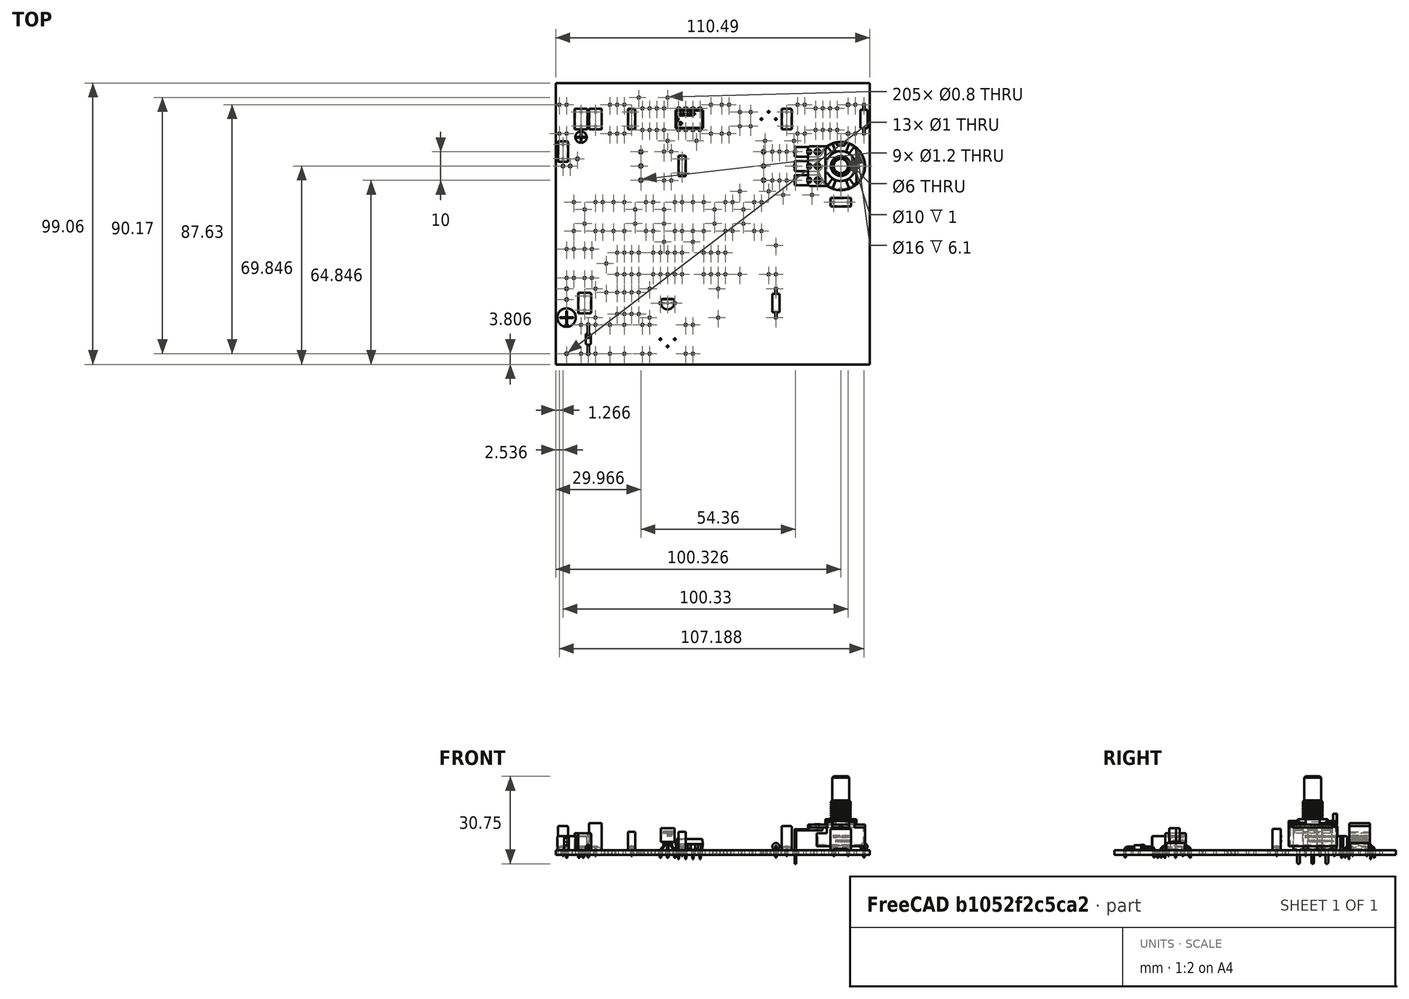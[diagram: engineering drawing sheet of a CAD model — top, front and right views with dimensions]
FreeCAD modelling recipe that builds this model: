
FCSTD DOCUMENT  (FreeCAD 0.19R17089 +1543 (Git))
Label: Board Reproduction
License: All rights reserved
LicenseURL: http://en.wikipedia.org/wiki/All_rights_reserved
objects: App::Link×70, Part::Feature×19, App::Part×4, PartDesign::CoordinateSystem×1, Sketcher::SketchObject×1
note: 21 computed .brp shape members not serialized (recipe doc carries the construction recipe); baked Part::Feature solids carry a one-line shape summary decoded from their .brp

FEATURE [PartDesign::CoordinateSystem] Local_CS
  AttacherType = Attacher::AttachEngine3D
FEATURE [Part::Feature] Pcb
  Placement = pos=(-148.5,98.5,0) rot=(0,0,1;0rad)
  shape: bbox 110.5 x 99.06 x 1.6 mm, 246 faces (baked)
FEATURE [Sketcher::SketchObject] PCB_Sketch
  sketch-geometry (10):
    g0: LineSegment StartX=-61.124 StartY=53.796 StartZ=0 EndX=-61.124 EndY=52.526 EndZ=0
    g1: LineSegment StartX=-25.564 StartY=53.796 StartZ=0 EndX=-61.124 EndY=53.796 EndZ=0
    g2: LineSegment StartX=49.366 StartY=53.796 StartZ=0 EndX=-25.564 EndY=53.796 EndZ=0
    g3: LineSegment StartX=49.366 StartY=-45.264 StartZ=0 EndX=49.366 EndY=53.796 EndZ=0
    g4: LineSegment StartX=-5.244 StartY=-45.264 StartZ=0 EndX=49.366 EndY=-45.264 EndZ=0
    g5: LineSegment StartX=-53.504 StartY=-45.264 StartZ=0 EndX=-5.244 EndY=-45.264 EndZ=0
    g6: LineSegment StartX=-61.124 StartY=-45.264 StartZ=0 EndX=-53.504 EndY=-45.264 EndZ=0
    g7: LineSegment StartX=-61.124 StartY=-38.914 StartZ=0 EndX=-61.124 EndY=-45.264 EndZ=0
    g8: LineSegment StartX=-61.124 StartY=1.726 StartZ=0 EndX=-61.124 EndY=52.526 EndZ=0
    g9: LineSegment StartX=-61.124 StartY=-38.914 StartZ=0 EndX=-61.124 EndY=1.726 EndZ=0
  constraints (10):
    c: Coincident(g6,g7)
    c: Coincident(g7,g9)
    c: Coincident(g8,g9)
    c: Coincident(g0,g8)
    c: Coincident(g0,g1)
    c: Coincident(g5,g6)
    c: Coincident(g1,g2)
    c: Coincident(g4,g5)
    c: Coincident(g3,g4)
    c: Coincident(g2,g3)
FEATURE [Part::Feature] Shape  label="C15_Nichicon_UMA_Straight_D6.5_H5_P2.5_d0.45_LL2.6_5D8C32D9"
  Placement = pos=(-57.314,-28.754,0) rot=(0,0,1;3.14159rad)
  shape: bbox 7.036 x 7.036 x 7.61 mm, 57 faces (baked)
FEATURE [Part::Feature] Shape001  label="C13_Nichicon_UMA_Straight_D4_H5_P1.5_d0.45_LL2.6_5D8A0658"
  Placement = pos=(-52.234,34.746,0) rot=(0,0,-1;1.5708rad)
  shape: bbox 4.33 x 4.33 x 7.61 mm, 61 faces (baked)
FEATURE [Part::Feature] Shape002  label="Q1_2N3904TAR_5D8C3344"
  Placement = pos=(-21.754,-23.674,0) rot=(0,0,1;3.14159rad)
  shape: bbox 5.54 x 3.625 x 10.42 mm, 233 faces (baked)
FEATURE [Part::Feature] Shape003  label="JP12_R_CF25_P10.16_H_5D8B2718"
  Placement = pos=(16.346,-23.674,0) rot=(0,0,1;1.5708rad)
  shape: bbox 2.5 x 10.96 x 5.1 mm, 11 faces (baked)
FEATURE [App::Link] JP12_R_CF25_P10_16_H_5D8B2718_ln_  label="JP11_R_CF25_P10.16_H_5D8B2701"
  LinkPlacement = pos=(23.966,14.426,0) rot=(0,0,1;3.14159rad)
  LinkedObject = -> Shape003
  Placement = pos=(23.966,14.426,0) rot=(0,0,1;3.14159rad)
FEATURE [App::Link] JP12_R_CF25_P10_16_H_5D8B2718_ln_001  label="JP10_R_CF25_P10.16_H_5D8B26EA"
  LinkPlacement = pos=(8.726,15.696,0) rot=(0,0,1;3.14159rad)
  LinkedObject = -> Shape003
  Placement = pos=(8.726,15.696,0) rot=(0,0,1;3.14159rad)
FEATURE [App::Link] JP12_R_CF25_P10_16_H_5D8B2718_ln_002  label="JP9_R_CF25_P10.16_H_5D8DF354"
  LinkPlacement = pos=(16.346,-8.434,0) rot=(0,0,1;1.5708rad)
  LinkedObject = -> Shape003
  Placement = pos=(16.346,-8.434,0) rot=(0,0,1;1.5708rad)
FEATURE [App::Link] JP12_R_CF25_P10_16_H_5D8B2718_ln_003  label="JP8_R_CF25_P10.16_H_5D8C9031"
  LinkPlacement = pos=(8.726,-13.514,0) rot=(0,0,1;3.14159rad)
  LinkedObject = -> Shape003
  Placement = pos=(8.726,-13.514,0) rot=(0,0,1;3.14159rad)
FEATURE [App::Link] JP12_R_CF25_P10_16_H_5D8B2718_ln_004  label="JP7_R_CF25_P10.16_H_5D8C3305"
  LinkPlacement = pos=(-3.974,-23.674,0) rot=(0,0,-1;1.5708rad)
  LinkedObject = -> Shape003
  Placement = pos=(-3.974,-23.674,0) rot=(0,0,-1;1.5708rad)
FEATURE [App::Link] JP12_R_CF25_P10_16_H_5D8B2718_ln_005  label="JP6_R_CF25_P10.16_H_5D8B268E"
  LinkPlacement = pos=(-17.944,-2.084,0) rot=(0,0,1;3.14159rad)
  LinkedObject = -> Shape003
  Placement = pos=(-17.944,-2.084,0) rot=(0,0,1;3.14159rad)
FEATURE [App::Link] JP12_R_CF25_P10_16_H_5D8B2718_ln_006  label="JP5_R_CF25_P10.16_H_5D8B2677"
  LinkPlacement = pos=(-28.104,-23.674,0) rot=(0,0,1;1.5708rad)
  LinkedObject = -> Shape003
  Placement = pos=(-28.104,-23.674,0) rot=(0,0,1;1.5708rad)
FEATURE [App::Link] JP12_R_CF25_P10_16_H_5D8B2718_ln_007  label="JP4_R_CF25_P10.16_H_5D8B2660"
  LinkPlacement = pos=(-43.344,-14.784,0) rot=(0,0,1;1.5708rad)
  LinkedObject = -> Shape003
  Placement = pos=(-43.344,-14.784,0) rot=(0,0,1;1.5708rad)
FEATURE [App::Link] JP12_R_CF25_P10_16_H_5D8B2718_ln_008  label="JP3_R_CF25_P10.16_H_5D8B2649"
  LinkPlacement = pos=(17.616,33.476,0) rot=(0,0,1;0rad)
  LinkedObject = -> Shape003
  Placement = pos=(17.616,33.476,0) rot=(0,0,1;0rad)
FEATURE [App::Link] JP12_R_CF25_P10_16_H_5D8B2718_ln_009  label="JP2_R_CF25_P10.16_H_5D8B2632"
  LinkPlacement = pos=(-16.674,33.476,0) rot=(0,0,1;0rad)
  LinkedObject = -> Shape003
  Placement = pos=(-16.674,33.476,0) rot=(0,0,1;0rad)
FEATURE [App::Link] JP12_R_CF25_P10_16_H_5D8B2718_ln_010  label="JP1_R_CF25_P10.16_H_5D8B261B"
  LinkPlacement = pos=(-26.834,48.716,0) rot=(0,0,1;0rad)
  LinkedObject = -> Shape003
  Placement = pos=(-26.834,48.716,0) rot=(0,0,1;0rad)
FEATURE [Part::Feature] Shape004  label="R57_R_CC25_P10.16_H_5D8A0B50"
  Placement = pos=(47.334,41.096,0) rot=(0,0,1;1.5708rad)
  shape: bbox 2.5 x 10.96 x 5.1 mm, 11 faces (baked)
FEATURE [App::Link] R57_R_CC25_P10_16_H_5D8A0B50_ln_  label="R56_R_CC25_P10.16_H_5D8A0B39"
  LinkPlacement = pos=(44.286,41.096,0) rot=(0,0,-1;1.5708rad)
  LinkedObject = -> Shape004
  Placement = pos=(44.286,41.096,0) rot=(0,0,-1;1.5708rad)
FEATURE [App::Link] R57_R_CC25_P10_16_H_5D8A0B50_ln_001  label="R45_R_CC25_P10.16_H_5D8A0B22"
  LinkPlacement = pos=(-28.104,-36.374,0) rot=(0,0,-1;1.5708rad)
  LinkedObject = -> Shape004
  Placement = pos=(-28.104,-36.374,0) rot=(0,0,-1;1.5708rad)
FEATURE [App::Link] R57_R_CC25_P10_16_H_5D8A0B50_ln_002  label="R44_R_CC25_P10.16_H_5D8A0B0B"
  LinkPlacement = pos=(-47.154,-36.374,0) rot=(0,0,-1;1.5708rad)
  LinkedObject = -> Shape004
  Placement = pos=(-47.154,-36.374,0) rot=(0,0,-1;1.5708rad)
FEATURE [App::Link] R57_R_CC25_P10_16_H_5D8A0B50_ln_003  label="R43_R_CC25_P10.16_H_5D8A0AF4"
  LinkPlacement = pos=(-30.644,-36.374,0) rot=(0,0,-1;1.5708rad)
  LinkedObject = -> Shape004
  Placement = pos=(-30.644,-36.374,0) rot=(0,0,-1;1.5708rad)
FEATURE [App::Link] R57_R_CC25_P10_16_H_5D8A0B50_ln_004  label="R42_R_CC25_P10.16_H_5D8BE438"
  LinkPlacement = pos=(-42.074,-36.374,0) rot=(0,0,-1;1.5708rad)
  LinkedObject = -> Shape004
  Placement = pos=(-42.074,-36.374,0) rot=(0,0,-1;1.5708rad)
FEATURE [App::Link] R57_R_CC25_P10_16_H_5D8A0B50_ln_005  label="R41_R_CC25_P10.16_H_5D8A0AC6"
  LinkPlacement = pos=(-36.994,-36.374,0) rot=(0,0,-1;1.5708rad)
  LinkedObject = -> Shape004
  Placement = pos=(-36.994,-36.374,0) rot=(0,0,-1;1.5708rad)
FEATURE [App::Link] R57_R_CC25_P10_16_H_5D8A0B50_ln_006  label="R39_R_CC25_P10.16_H_5D8A0AAF"
  LinkPlacement = pos=(-15.404,-36.374,0) rot=(0,0,-1;1.5708rad)
  LinkedObject = -> Shape004
  Placement = pos=(-15.404,-36.374,0) rot=(0,0,-1;1.5708rad)
FEATURE [App::Link] R57_R_CC25_P10_16_H_5D8A0B50_ln_007  label="R37_R_CC25_P10.16_H_5D8A0A98"
  LinkPlacement = pos=(-12.864,-36.374,0) rot=(0,0,-1;1.5708rad)
  LinkedObject = -> Shape004
  Placement = pos=(-12.864,-36.374,0) rot=(0,0,-1;1.5708rad)
FEATURE [App::Link] R57_R_CC25_P10_16_H_5D8A0B50_ln_008  label="R36_R_CC25_P10.16_H_5D8A0A81"
  LinkPlacement = pos=(15.076,24.586,0) rot=(0,0,-1;1.5708rad)
  LinkedObject = -> Shape004
  Placement = pos=(15.076,24.586,0) rot=(0,0,-1;1.5708rad)
FEATURE [App::Link] R57_R_CC25_P10_16_H_5D8A0B50_ln_009  label="R35_R_CC25_P10.16_H_5D8A0A6A"
  LinkPlacement = pos=(20.156,24.586,0) rot=(0,0,-1;1.5708rad)
  LinkedObject = -> Shape004
  Placement = pos=(20.156,24.586,0) rot=(0,0,-1;1.5708rad)
FEATURE [App::Link] R57_R_CC25_P10_16_H_5D8A0B50_ln_010  label="R34_R_CC25_P10.16_H_5D8A0A53"
  LinkPlacement = pos=(17.616,24.586,0) rot=(0,0,-1;1.5708rad)
  LinkedObject = -> Shape004
  Placement = pos=(17.616,24.586,0) rot=(0,0,-1;1.5708rad)
FEATURE [App::Link] R57_R_CC25_P10_16_H_5D8A0B50_ln_011  label="R33_R_CC25_P10.16_H_5D8A0A3C"
  LinkPlacement = pos=(26.506,41.096,0) rot=(0,0,1;1.5708rad)
  LinkedObject = -> Shape004
  Placement = pos=(26.506,41.096,0) rot=(0,0,1;1.5708rad)
FEATURE [App::Link] R57_R_CC25_P10_16_H_5D8A0B50_ln_012  label="R32_R_CC25_P10.16_H_5D8A0A25"
  LinkPlacement = pos=(23.966,41.096,0) rot=(0,0,-1;1.5708rad)
  LinkedObject = -> Shape004
  Placement = pos=(23.966,41.096,0) rot=(0,0,-1;1.5708rad)
FEATURE [App::Link] R57_R_CC25_P10_16_H_5D8A0B50_ln_013  label="R31_R_CC25_P10.16_H_5D8A0A0E"
  LinkPlacement = pos=(-52.234,-36.374,0) rot=(0,0,-1;1.5708rad)
  LinkedObject = -> Shape004
  Placement = pos=(-52.234,-36.374,0) rot=(0,0,-1;1.5708rad)
FEATURE [App::Link] R57_R_CC25_P10_16_H_5D8A0B50_ln_014  label="R30_R_CC25_P10.16_H_5D8C3383"
  LinkPlacement = pos=(-47.154,-23.674,0) rot=(0,0,1;1.5708rad)
  LinkedObject = -> Shape004
  Placement = pos=(-47.154,-23.674,0) rot=(0,0,1;1.5708rad)
FEATURE [App::Link] R57_R_CC25_P10_16_H_5D8A0B50_ln_015  label="R29_R_CC25_P10.16_H_5D8A09E0"
  LinkPlacement = pos=(-54.774,-9.704,0) rot=(0,0,-1;1.5708rad)
  LinkedObject = -> Shape004
  Placement = pos=(-54.774,-9.704,0) rot=(0,0,-1;1.5708rad)
FEATURE [App::Link] R57_R_CC25_P10_16_H_5D8A0B50_ln_016  label="R28_R_CC25_P10.16_H_5D8A09C9"
  LinkPlacement = pos=(-57.314,-9.704,0) rot=(0,0,1;1.5708rad)
  LinkedObject = -> Shape004
  Placement = pos=(-57.314,-9.704,0) rot=(0,0,1;1.5708rad)
FEATURE [App::Link] R57_R_CC25_P10_16_H_5D8A0B50_ln_017  label="R27_R_CC25_P10.16_H_5D8A09B2"
  LinkPlacement = pos=(-50.964,-9.704,0) rot=(0,0,1;1.5708rad)
  LinkedObject = -> Shape004
  Placement = pos=(-50.964,-9.704,0) rot=(0,0,1;1.5708rad)
FEATURE [App::Link] R57_R_CC25_P10_16_H_5D8A0B50_ln_018  label="R26_R_CC25_P10.16_H_5D8A099B"
  LinkPlacement = pos=(-48.424,-9.704,0) rot=(0,0,1;1.5708rad)
  LinkedObject = -> Shape004
  Placement = pos=(-48.424,-9.704,0) rot=(0,0,1;1.5708rad)
FEATURE [App::Link] R57_R_CC25_P10_16_H_5D8A0B50_ln_019  label="R25_R_CC25_P10.16_H_5D8B716B"
  LinkPlacement = pos=(11.266,6.806,0) rot=(0,0,-1;1.5708rad)
  LinkedObject = -> Shape004
  Placement = pos=(11.266,6.806,0) rot=(0,0,-1;1.5708rad)
FEATURE [App::Link] R57_R_CC25_P10_16_H_5D8A0B50_ln_020  label="R24_R_CC25_P10.16_H_5D8A096D"
  LinkPlacement = pos=(-0.164,41.096,0) rot=(0,0,1;1.5708rad)
  LinkedObject = -> Shape004
  Placement = pos=(-0.164,41.096,0) rot=(0,0,1;1.5708rad)
FEATURE [App::Link] R57_R_CC25_P10_16_H_5D8A0B50_ln_021  label="R23_R_CC25_P10.16_H_5D8A0956"
  LinkPlacement = pos=(-2.704,41.096,0) rot=(0,0,-1;1.5708rad)
  LinkedObject = -> Shape004
  Placement = pos=(-2.704,41.096,0) rot=(0,0,-1;1.5708rad)
FEATURE [App::Link] R57_R_CC25_P10_16_H_5D8A0B50_ln_022  label="R22_R_CC25_P10.16_H_5D8B6ED7"
  LinkPlacement = pos=(8.726,6.806,0) rot=(0,0,-1;1.5708rad)
  LinkedObject = -> Shape004
  Placement = pos=(8.726,6.806,0) rot=(0,0,-1;1.5708rad)
FEATURE [App::Link] R57_R_CC25_P10_16_H_5D8A0B50_ln_023  label="R21_R_CC25_P10.16_H_5D8A0928"
  LinkPlacement = pos=(-6.514,41.096,0) rot=(0,0,-1;1.5708rad)
  LinkedObject = -> Shape004
  Placement = pos=(-6.514,41.096,0) rot=(0,0,-1;1.5708rad)
FEATURE [App::Link] R57_R_CC25_P10_16_H_5D8A0B50_ln_024  label="R20_R_CC25_P10.16_H_5D8B7021"
  LinkPlacement = pos=(1.106,6.806,0) rot=(0,0,-1;1.5708rad)
  LinkedObject = -> Shape004
  Placement = pos=(1.106,6.806,0) rot=(0,0,-1;1.5708rad)
FEATURE [App::Link] R57_R_CC25_P10_16_H_5D8A0B50_ln_025  label="R19_R_CC25_P10.16_H_5D8C3024"
  LinkPlacement = pos=(-1.434,6.806,0) rot=(0,0,1;1.5708rad)
  LinkedObject = -> Shape004
  Placement = pos=(-1.434,6.806,0) rot=(0,0,1;1.5708rad)
FEATURE [App::Link] R57_R_CC25_P10_16_H_5D8A0B50_ln_026  label="R18_R_CC25_P10.16_H_5D8B70E7"
  LinkPlacement = pos=(-9.054,6.806,0) rot=(0,0,-1;1.5708rad)
  LinkedObject = -> Shape004
  Placement = pos=(-9.054,6.806,0) rot=(0,0,-1;1.5708rad)
FEATURE [App::Link] R57_R_CC25_P10_16_H_5D8A0B50_ln_027  label="R17_R_CC25_P10.16_H_5D8B6E95"
  LinkPlacement = pos=(-12.864,6.806,0) rot=(0,0,-1;1.5708rad)
  LinkedObject = -> Shape004
  Placement = pos=(-12.864,6.806,0) rot=(0,0,-1;1.5708rad)
FEATURE [App::Link] R57_R_CC25_P10_16_H_5D8A0B50_ln_028  label="R16_R_CC25_P10.16_H_5D8B6F9D"
  LinkPlacement = pos=(-19.214,6.806,0) rot=(0,0,1;1.5708rad)
  LinkedObject = -> Shape004
  Placement = pos=(-19.214,6.806,0) rot=(0,0,1;1.5708rad)
FEATURE [App::Link] R57_R_CC25_P10_16_H_5D8A0B50_ln_029  label="R15_R_CC25_P10.16_H_5D8B6FDF"
  LinkPlacement = pos=(-16.674,6.806,0) rot=(0,0,-1;1.5708rad)
  LinkedObject = -> Shape004
  Placement = pos=(-16.674,6.806,0) rot=(0,0,-1;1.5708rad)
FEATURE [App::Link] R57_R_CC25_P10_16_H_5D8A0B50_ln_030  label="R14_R_CC25_P10.16_H_5D8B7063"
  LinkPlacement = pos=(-26.834,6.806,0) rot=(0,0,-1;1.5708rad)
  LinkedObject = -> Shape004
  Placement = pos=(-26.834,6.806,0) rot=(0,0,-1;1.5708rad)
FEATURE [App::Link] R57_R_CC25_P10_16_H_5D8A0B50_ln_031  label="R13_R_CC25_P10.16_H_5D8B7129"
  LinkPlacement = pos=(-29.374,6.806,0) rot=(0,0,1;1.5708rad)
  LinkedObject = -> Shape004
  Placement = pos=(-29.374,6.806,0) rot=(0,0,1;1.5708rad)
FEATURE [App::Link] R57_R_CC25_P10_16_H_5D8A0B50_ln_032  label="R12_R_CC25_P10.16_H_5D8B70A5"
  LinkPlacement = pos=(-36.994,6.806,0) rot=(0,0,-1;1.5708rad)
  LinkedObject = -> Shape004
  Placement = pos=(-36.994,6.806,0) rot=(0,0,-1;1.5708rad)
FEATURE [App::Link] R57_R_CC25_P10_16_H_5D8A0B50_ln_033  label="R11_R_CC25_P10.16_H_5D8B6F5B"
  LinkPlacement = pos=(-40.804,6.806,0) rot=(0,0,-1;1.5708rad)
  LinkedObject = -> Shape004
  Placement = pos=(-40.804,6.806,0) rot=(0,0,-1;1.5708rad)
FEATURE [App::Link] R57_R_CC25_P10_16_H_5D8A0B50_ln_034  label="R10_R_CC25_P10.16_H_5D8A082B"
  LinkPlacement = pos=(-54.774,6.806,0) rot=(0,0,1;1.5708rad)
  LinkedObject = -> Shape004
  Placement = pos=(-54.774,6.806,0) rot=(0,0,1;1.5708rad)
FEATURE [App::Link] R57_R_CC25_P10_16_H_5D8A0B50_ln_035  label="R9_R_CC25_P10.16_H_5D8A0814"
  LinkPlacement = pos=(-44.614,6.806,0) rot=(0,0,-1;1.5708rad)
  LinkedObject = -> Shape004
  Placement = pos=(-44.614,6.806,0) rot=(0,0,-1;1.5708rad)
FEATURE [App::Link] R57_R_CC25_P10_16_H_5D8A0B50_ln_036  label="R8_R_CC25_P10.16_H_5D8A07FD"
  LinkPlacement = pos=(-47.154,6.806,0) rot=(0,0,1;1.5708rad)
  LinkedObject = -> Shape004
  Placement = pos=(-47.154,6.806,0) rot=(0,0,1;1.5708rad)
FEATURE [App::Link] R57_R_CC25_P10_16_H_5D8A0B50_ln_037  label="R7_R_CC25_P10.16_H_5D8A07E6"
  LinkPlacement = pos=(-23.024,24.586,0) rot=(0,0,1;1.5708rad)
  LinkedObject = -> Shape004
  Placement = pos=(-23.024,24.586,0) rot=(0,0,1;1.5708rad)
FEATURE [App::Link] R57_R_CC25_P10_16_H_5D8A0B50_ln_038  label="R6_R_CC25_P10.16_H_5D8A07CF"
  LinkPlacement = pos=(-20.484,24.586,0) rot=(0,0,-1;1.5708rad)
  LinkedObject = -> Shape004
  Placement = pos=(-20.484,24.586,0) rot=(0,0,-1;1.5708rad)
FEATURE [App::Link] R57_R_CC25_P10_16_H_5D8A0B50_ln_039  label="R5_R_CC25_P10.16_H_5D8A07B8"
  LinkPlacement = pos=(-36.994,41.096,0) rot=(0,0,-1;1.5708rad)
  LinkedObject = -> Shape004
  Placement = pos=(-36.994,41.096,0) rot=(0,0,-1;1.5708rad)
FEATURE [App::Link] R57_R_CC25_P10_16_H_5D8A0B50_ln_040  label="R4_R_CC25_P10.16_H_5D8A07A1"
  LinkPlacement = pos=(-39.534,41.096,0) rot=(0,0,-1;1.5708rad)
  LinkedObject = -> Shape004
  Placement = pos=(-39.534,41.096,0) rot=(0,0,-1;1.5708rad)
FEATURE [App::Link] R57_R_CC25_P10_16_H_5D8A0B50_ln_041  label="R3_R_CC25_P10.16_H_5D8A078A"
  LinkPlacement = pos=(-42.074,41.096,0) rot=(0,0,-1;1.5708rad)
  LinkedObject = -> Shape004
  Placement = pos=(-42.074,41.096,0) rot=(0,0,-1;1.5708rad)
FEATURE [App::Link] R57_R_CC25_P10_16_H_5D8A0B50_ln_042  label="R2_R_CC25_P10.16_H_5D8C237F"
  LinkPlacement = pos=(-57.314,41.096,0) rot=(0,0,1;1.5708rad)
  LinkedObject = -> Shape004
  Placement = pos=(-57.314,41.096,0) rot=(0,0,1;1.5708rad)
FEATURE [App::Link] R57_R_CC25_P10_16_H_5D8A0B50_ln_043  label="R1_R_CC25_P10.16_H_5D8A075C"
  LinkPlacement = pos=(-59.854,41.096,0) rot=(0,0,-1;1.5708rad)
  LinkedObject = -> Shape004
  Placement = pos=(-59.854,41.096,0) rot=(0,0,-1;1.5708rad)
FEATURE [Part::Feature] Shape005  label="U4_RC4558P_5D8A747F"
  Placement = pos=(-14.134,41.096,0) rot=(0,0,1;1.5708rad)
  shape: bbox 9.59 x 7.87 x 7.1 mm, 280 faces (baked)
FEATURE [App::Link] U4_RC4558P_5D8A747F_ln_  label="U3_RC4558P_5D8A7463"
  LinkPlacement = pos=(-5.244,-9.704,0) rot=(0,0,1;1.5708rad)
  LinkedObject = -> Shape005
  Placement = pos=(-5.244,-9.704,0) rot=(0,0,1;1.5708rad)
FEATURE [App::Link] U4_RC4558P_5D8A747F_ln_001  label="U2_RC4558P_5D8A7447"
  LinkPlacement = pos=(-35.724,-9.704,0) rot=(0,0,1;1.5708rad)
  LinkedObject = -> Shape005
  Placement = pos=(-35.724,-9.704,0) rot=(0,0,1;1.5708rad)
FEATURE [App::Link] U4_RC4558P_5D8A747F_ln_002  label="U6_RC4558P_5D8A0CCA"
  LinkPlacement = pos=(34.126,41.096,0) rot=(0,0,1;1.5708rad)
  LinkedObject = -> Shape005
  Placement = pos=(34.126,41.096,0) rot=(0,0,1;1.5708rad)
FEATURE [App::Link] U4_RC4558P_5D8A747F_ln_003  label="U5_RC4558P_5D8C3250"
  LinkPlacement = pos=(-35.724,-23.674,0) rot=(0,0,1;1.5708rad)
  LinkedObject = -> Shape005
  Placement = pos=(-35.724,-23.674,0) rot=(0,0,1;1.5708rad)
FEATURE [App::Link] U4_RC4558P_5D8A747F_ln_004  label="U1_RC4558P_5D8A0C3E"
  LinkPlacement = pos=(-26.834,41.096,0) rot=(0,0,1;1.5708rad)
  LinkedObject = -> Shape005
  Placement = pos=(-26.834,41.096,0) rot=(0,0,1;1.5708rad)
FEATURE [Part::Feature] Shape006  label="RV55_RV16AF-41-15R_5D8A0C22"
  Placement = pos=(39.206,24.586,9) rot=(0,0,-1;1.5708rad)
  shape: bbox 24.75 x 17.02 x 30.75 mm, 441 faces, 7 solids (baked)
FEATURE [App::Link] RV55_RV16AF_41_15R_5D8A0C22_ln_  label="RV54_RV16AF-41-15R_5D8A0C04"
  LinkPlacement = pos=(-3.974,24.586,9) rot=(0,0,1;1.5708rad)
  LinkedObject = -> Shape006
  Placement = pos=(-3.974,24.586,9) rot=(0,0,1;1.5708rad)
FEATURE [App::Link] RV55_RV16AF_41_15R_5D8A0C22_ln_001  label="RV53_RV16AF-41-15R_5D8C0692"
  LinkPlacement = pos=(-47.154,24.586,9) rot=(0,0,1;1.5708rad)
  LinkedObject = -> Shape006
  Placement = pos=(-47.154,24.586,9) rot=(0,0,1;1.5708rad)
FEATURE [Part::Feature] Shape007  label="D9_DO-35_P10.16_5D8A06C2"
  Placement = pos=(-49.694,-36.374,0) rot=(0,0,1;1.5708rad)
  shape: bbox 1.862 x 10.84 x 4.391 mm, 17 faces (baked)
FEATURE [App::Link] D9_DO_35_P10_16_5D8A06C2_ln_  label="D8_DO-35_P10.16_5D8A06B3"
  LinkPlacement = pos=(41.746,41.096,0) rot=(0,0,1;1.5708rad)
  LinkedObject = -> Shape007
  Placement = pos=(41.746,41.096,0) rot=(0,0,1;1.5708rad)
FEATURE [Part::Feature] Shape008  label="C23_FKS2G016801B00KSSD_5D8A06A4"
  Placement = pos=(39.206,11.886,0) rot=(0,0,1;3.14159rad)
  shape: bbox 15.3 x 3.9 x 9.5 mm, 432 faces (baked)
FEATURE [Part::Feature] Shape009  label="C16_MKS2C034701C00KSSD_5D8A0691"
  Placement = pos=(20.156,41.096,0) rot=(0,0,-1;1.5708rad)
  shape: bbox 4.65 x 15.3 x 10.5 mm, 395 faces (baked)
FEATURE [Part::Feature] Shape010  label="C14_FKP2J006801D00JSSD_5D8C32AA"
  Placement = pos=(-50.964,-23.674,0) rot=(0,0,-1;1.5708rad)
  shape: bbox 6.15 x 15.3 x 8 mm, 402 faces (baked)
FEATURE [App::Link] C16_MKS2C034701C00KSSD_5D8A0691_ln_  label="C12_MKS2C034701C00KSSD_5D8A0645"
  LinkPlacement = pos=(7.456,41.096,0) rot=(0,0,1;1.5708rad)
  LinkedObject = -> Shape009
  Placement = pos=(7.456,41.096,0) rot=(0,0,1;1.5708rad)
FEATURE [App::Link] C23_FKS2G016801B00KSSD_5D8A06A4_ln_  label="C11_FKS2G016801B00KSSD_5D8A0632"
  LinkPlacement = pos=(3.646,41.096,0) rot=(0,0,1;1.5708rad)
  LinkedObject = -> Shape008
  Placement = pos=(3.646,41.096,0) rot=(0,0,1;1.5708rad)
FEATURE [App::Link] C23_FKS2G016801B00KSSD_5D8A06A4_ln_001  label="C10_FKS2G016801B00KSSD_5D8B724B"
  LinkPlacement = pos=(4.916,6.806,0) rot=(0,0,1;1.5708rad)
  LinkedObject = -> Shape008
  Placement = pos=(4.916,6.806,0) rot=(0,0,1;1.5708rad)
FEATURE [App::Link] C23_FKS2G016801B00KSSD_5D8A06A4_ln_002  label="C9_FKS2G016801B00KSSD_5D8B7215"
  LinkPlacement = pos=(-5.244,6.806,0) rot=(0,0,-1;1.5708rad)
  LinkedObject = -> Shape008
  Placement = pos=(-5.244,6.806,0) rot=(0,0,-1;1.5708rad)
FEATURE [App::Link] C23_FKS2G016801B00KSSD_5D8A06A4_ln_003  label="C8_FKS2G016801B00KSSD_5D8B71DF"
  LinkPlacement = pos=(-23.024,6.806,0) rot=(0,0,-1;1.5708rad)
  LinkedObject = -> Shape008
  Placement = pos=(-23.024,6.806,0) rot=(0,0,-1;1.5708rad)
FEATURE [App::Link] C23_FKS2G016801B00KSSD_5D8A06A4_ln_004  label="C7_FKS2G016801B00KSSD_5D8B71A9"
  LinkPlacement = pos=(-33.184,6.806,0) rot=(0,0,-1;1.5708rad)
  LinkedObject = -> Shape008
  Placement = pos=(-33.184,6.806,0) rot=(0,0,-1;1.5708rad)
FEATURE [App::Link] C23_FKS2G016801B00KSSD_5D8A06A4_ln_005  label="C6_FKS2G016801B00KSSD_5D8A05D3"
  LinkPlacement = pos=(-50.964,6.806,0) rot=(0,0,-1;1.5708rad)
  LinkedObject = -> Shape008
  Placement = pos=(-50.964,6.806,0) rot=(0,0,-1;1.5708rad)
FEATURE [Part::Feature] Shape011  label="C5_FKS2G013301A00KSSD_5D8A05C0"
  Placement = pos=(-16.674,24.586,0) rot=(0,0,-1;1.5708rad)
  shape: bbox 3.15 x 15.3 x 8.5 mm, 428 faces (baked)
FEATURE [Part::Feature] Shape012  label="C4_FKS2G011001A00KSSD_5D8A05AD"
  Placement = pos=(-34.454,41.096,0) rot=(0,0,1;1.5708rad)
  shape: bbox 3.15 x 15.3 x 8.5 mm, 398 faces (baked)
FEATURE [Part::Feature] Shape013  label="C3_MKS2F031001E00KSSD_5D8A059A"
  Placement = pos=(-47.154,41.096,0) rot=(0,0,-1;1.5708rad)
  shape: bbox 6.15 x 15.3 x 11.5 mm, 409 faces (baked)
FEATURE [Part::Feature] Shape014  label="C2_FKP2J001001D00JSSD_5D8A0587"
  Placement = pos=(-52.234,41.096,0) rot=(0,0,-1;1.5708rad)
  shape: bbox 6.15 x 15.3 x 8 mm, 368 faces (baked)
FEATURE [Part::Feature] Shape015  label="C1_MKS2F024701C00KSSD_5D8A0574"
  Placement = pos=(-58.584,29.666,0) rot=(0,0,1;1.5708rad)
  shape: bbox 4.65 x 15.3 x 10.5 mm, 401 faces (baked)
FEATURE [App::Part] Top
  Group = -> [Shape,Shape001,Shape002,Shape003,JP12_R_CF25_P10_16_H_5D8B2718_ln_,JP12_R_CF25_P10_16_H_5D8B2718_ln_001,JP12_R_CF25_P10_16_H_5D8B2718_ln_002,JP12_R_CF25_P10_16_H_5D8B2718_ln_003,JP12_R_CF25_P10_16_H_5D8B2718_ln_004,JP12_R_CF25_P10_16_H_5D8B2718_ln_005,JP12_R_CF25_P10_16_H_5D8B2718_ln_006,JP12_R_CF25_P10_16_H_5D8B2718_ln_007,JP12_R_CF25_P10_16_H_5D8B2718_ln_008,JP12_R_CF25_P10_16_H_5D8B2718_ln_009,+72 more]
  Origin = -> Origin003
FEATURE [App::Part] Step_Models
  Group = -> [Top]
  Origin = -> Origin002
FEATURE [Part::Feature] topTracks
  Placement = pos=(-148.5,98.5,0.01) rot=(0,0,1;0rad)
  shape: bbox 108.8 x 91.81 x 0.04 mm, 247 faces, 0 solids (baked)
FEATURE [Part::Feature] botTracks
  Placement = pos=(-148.5,98.5,-1.61) rot=(0,0,1;0rad)
  shape: bbox 109.8 x 97.28 x 0.02 mm, 303 faces, 0 solids (baked)
FEATURE [App::Part] Board_Geoms
  Group = -> [Local_CS,Pcb,PCB_Sketch,topTracks,botTracks]
  Origin = -> Origin
FEATURE [App::Part] Board  label="Board Reproduction"
  Group = -> [Board_Geoms,Step_Models]
  Origin = -> Origin001
